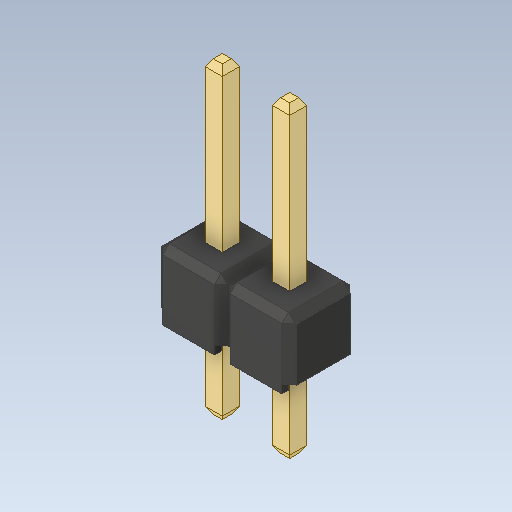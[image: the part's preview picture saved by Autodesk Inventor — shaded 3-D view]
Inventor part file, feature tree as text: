
AUTODESK INVENTOR PART (.ipt)
format: ipt  version: 2020 (Build 240168000, 168)  size: 146,432 bytes
history: native  units: in
note: dims shown in document units (in); Inventor stores cm internally (conversion verified against a paired STEP export)
features: other x3, chamfer x1
ambient origin geometry x8: Origin, YZ Plane, XZ Plane, XY Plane, X Axis, Y Axis, Z Axis, Center Point
bodies: Solid1 (feature_tree), Solid2 (feature_tree), Solid3 (feature_tree), Solid4 (feature_tree)
feature tree (4):
  chamfer  "Chamfer2"  [1 undecoded]
  other  "Boss-Extrude3"
  other  "LPattern1[1]"
  other  "LPattern1[2]"
note: 1 required parameter value undecoded (feature->parameter linkage not recoverable at this tier; creation-order binding heuristic only, values carry confidence <= 0.55)
